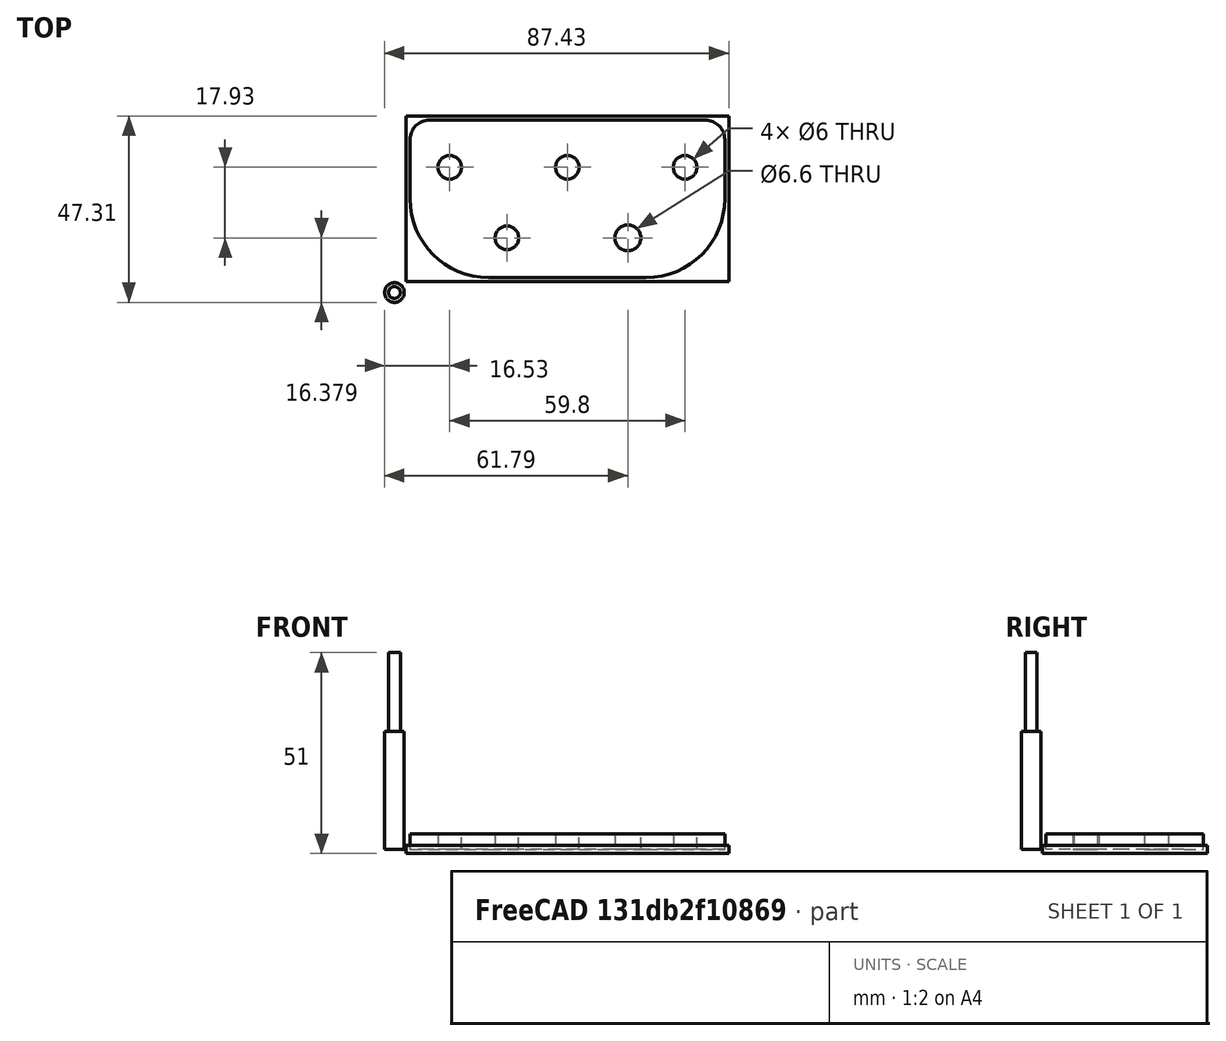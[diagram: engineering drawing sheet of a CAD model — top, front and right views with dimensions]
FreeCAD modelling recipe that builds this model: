
FCSTD DOCUMENT  (FreeCAD 1.0R39319 (Git))
Label: HousingAtari_MINI_BUTTONS_RETROFIT
License: All rights reserved
LicenseURL: https://en.wikipedia.org/wiki/All_rights_reserved
objects: App::DocumentObjectGroup×3, Path::FeaturePython×3, Sketcher::SketchObject×2, Part::FeaturePython×2, PartDesign::Pad×1, PartDesign::Body×1, App::FeaturePython×1, Part::Part2DObjectPython×1, Mesh::FeaturePython×1
note: 11 computed .brp shape members not serialized (recipe doc carries the construction recipe); baked Part::Feature solids carry a one-line shape summary decoded from their .brp

FEATURE [Sketcher::SketchObject] Sketch  label="A3"
  ArcFitTolerance = 0
  FullyConstrained = false
  MakeInternals = false
  MapMode = 5
  sketch-geometry (7):
    g0: LineSegment StartX=0 StartY=420 StartZ=0 EndX=0 EndY=0 EndZ=0
    g1: LineSegment StartX=0 StartY=420 StartZ=0 EndX=148.5 EndY=420 EndZ=0
    g2: LineSegment StartX=148.5 StartY=420 StartZ=0 EndX=148.5 EndY=0 EndZ=0
    g3: LineSegment StartX=148.5 StartY=420 StartZ=0 EndX=297 EndY=420 EndZ=0
    g4: LineSegment StartX=297 StartY=420 StartZ=0 EndX=297 EndY=210 EndZ=0
    g5: LineSegment StartX=297 StartY=210 StartZ=0 EndX=297 EndY=0 EndZ=0
    g6: LineSegment StartX=297 StartY=210 StartZ=0 EndX=0 EndY=210 EndZ=0
  constraints (21):
    c: Vertical(g0)
    c: DistanceY(g0,g0) = 420
    c: Coincident(g1,g0)
    c: Horizontal(g1)
    c: Coincident(g2,g1)
    c: Coincident(g3,g1)
    c: Horizontal(g3)
    c: Equal(g1,g3)
    c: Vertical(g2)
    c: DistanceX(g0,g3) = 297
    c: Coincident(g4,g3)
    c: Vertical(g4)
    c: Coincident(g5,g4)
    c: PointOnObject(g5,g-1)
    c: Vertical(g5)
    c: Equal(g5,g4)
    c: PointOnObject(g0,g-1)
    c: PointOnObject(g0,g-2)
    c: Coincident(g6,g4)
    c: PointOnObject(g6,g0)
    c: Horizontal(g6)
FEATURE [Sketcher::SketchObject] Sketch008  label="PART-mini_switches"
  ArcFitTolerance = 1e-06
  AttachmentSupport = -> [XY_Plane]
  FullyConstrained = false
  MakeInternals = false
  MapMode = 5
  sketch-geometry (24):
    g0: LineSegment StartX=3.9304 StartY=38.8086 StartZ=0 EndX=3.9304 EndY=23.8086 EndZ=0
    g1: LineSegment StartX=23.9304 StartY=3.80861 StartZ=0 EndX=63.9304 EndY=3.80861 EndZ=0
    g2: LineSegment StartX=83.9304 StartY=23.8086 StartZ=0 EndX=83.9304 EndY=38.8086 EndZ=0
    g3: LineSegment StartX=78.9304 StartY=43.8086 StartZ=0 EndX=8.9304 EndY=43.8086 EndZ=0
    g4: ArcOfCircle CenterX=23.9304 CenterY=23.8086 CenterZ=0 NormalX=0 NormalY=0 NormalZ=1 AngleXU=0 Radius=20 StartAngle=3.14159 EndAngle=4.71239
    g5: GeomPoint [constr] X=3.9304 Y=3.80861 Z=0
    g6: ArcOfCircle CenterX=63.9304 CenterY=23.8086 CenterZ=0 NormalX=0 NormalY=0 NormalZ=1 AngleXU=0 Radius=20 StartAngle=4.71239 EndAngle=6.28319
    g7: GeomPoint [constr] X=83.9304 Y=3.80861 Z=0
    g8: ArcOfCircle CenterX=78.9304 CenterY=38.8086 CenterZ=0 NormalX=0 NormalY=0 NormalZ=1 AngleXU=0 Radius=5 StartAngle=4e-16 EndAngle=1.5708
    g9: GeomPoint [constr] X=83.9304 Y=43.8086 Z=0
    g10: ArcOfCircle CenterX=8.9304 CenterY=38.8086 CenterZ=0 NormalX=0 NormalY=0 NormalZ=1 AngleXU=0 Radius=5 StartAngle=1.5708 EndAngle=3.14159
    g11: GeomPoint [constr] X=3.9304 Y=43.8086 Z=0
    g12: LineSegment [constr] StartX=14.0304 StartY=31.8086 StartZ=0 EndX=43.9304 EndY=31.8086 EndZ=0
    g13: LineSegment [constr] StartX=43.9304 StartY=31.8086 StartZ=0 EndX=73.8304 EndY=31.8086 EndZ=0
    g14: LineSegment [constr] StartX=73.8304 StartY=31.8086 StartZ=0 EndX=59.2902 EndY=13.8786 EndZ=0
    g15: LineSegment [constr] StartX=59.2902 StartY=13.8786 StartZ=0 EndX=28.5706 EndY=13.8786 EndZ=0
    g16: LineSegment [constr] StartX=28.5706 StartY=13.8786 StartZ=0 EndX=14.0304 EndY=31.8086 EndZ=0
    g17: Circle CenterX=14.0304 CenterY=31.8086 CenterZ=0 NormalX=0 NormalY=0 NormalZ=1 AngleXU=0 Radius=3
    g18: Circle CenterX=43.9304 CenterY=31.8086 CenterZ=0 NormalX=0 NormalY=0 NormalZ=1 AngleXU=0 Radius=3
    g19: Circle CenterX=73.8304 CenterY=31.8086 CenterZ=0 NormalX=0 NormalY=0 NormalZ=1 AngleXU=0 Radius=3
    g20: Circle CenterX=59.2902 CenterY=13.8786 CenterZ=0 NormalX=0 NormalY=0 NormalZ=1 AngleXU=0 Radius=3.30031
    g21: Circle CenterX=28.5706 CenterY=13.8786 CenterZ=0 NormalX=0 NormalY=0 NormalZ=1 AngleXU=0 Radius=3
    g22: LineSegment [constr] StartX=8.9304 StartY=43.8086 StartZ=0 EndX=43.9304 EndY=31.8086 EndZ=0
    g23: LineSegment [constr] StartX=78.9304 StartY=43.8086 StartZ=0 EndX=43.9304 EndY=31.8086 EndZ=0
  constraints (52):
    c: Vertical(g0)
    c: Vertical(g2)
    c: Horizontal(g1)
    c: Horizontal(g3)
    c: PointOnObject(g5,g0)
    c: PointOnObject(g5,g1)
    c: Tangent(g0,g4) = -1.5708
    c: Tangent(g1,g4) = -1.5708
    c: PointOnObject(g7,g1)
    c: PointOnObject(g7,g2)
    c: Tangent(g1,g6) = -1.5708
    c: Tangent(g2,g6) = -1.5708
    c: Radius(g4) = 20
    c: Equal(g6,g4)
    c: DistanceX(g0,g2) = 80
    c: PointOnObject(g9,g3)
    c: PointOnObject(g9,g2)
    c: Tangent(g3,g8) = -1.5708
    c: Tangent(g2,g8) = -1.5708
    c: PointOnObject(g11,g0)
    c: PointOnObject(g11,g3)
    c: Tangent(g0,g10) = -1.5708
    c: Tangent(g3,g10) = -1.5708
    c: Equal(g10,g8)
    c: Horizontal(g12)
    c: Coincident(g13,g12)
    c: Horizontal(g13)
    c: Coincident(g14,g13)
    c: Coincident(g15,g14)
    c: Horizontal(g15)
    c: Coincident(g16,g15)
    c: Equal(g16,g14)
    c: DistanceY(g1,g3) = 40
    c: Equal(g13,g12)
    c: Coincident(g16,g12)
    c: Coincident(g17,g12)
    c: Coincident(g18,g12)
    c: Coincident(g19,g13)
    c: Coincident(g20,g14)
    c: Coincident(g21,g15)
    c: Equal(g18,g19)
    c: Equal(g19,g21)
    c: Diameter(g17) = 6
    c: Equal(g17,g21)
    c: Coincident(g22,g3)
    c: Coincident(g22,g12)
    c: Coincident(g23,g3)
    c: Coincident(g23,g12)
    c: Equal(g23,g22)
    c: DistanceY(g12,g3) = 12
    c: DistanceY(g14,g13) = 17.93
    c: Radius(g8) = 5
FEATURE [PartDesign::Pad] Pad
  Direction = (0,0,1)
  Length = 4
  Length2 = 10
  Profile = -> Sketch008
  ReferenceAxis = -> Sketch008 [N_Axis]
  Refine = true
  Suppressed = false
  Type = 0
FEATURE [PartDesign::Body] Body
  AllowCompound = false
  Group = -> [Sketch,Pad,Sketch008]
  Origin = -> Origin
  Tip = -> Pad
FEATURE [App::FeaturePython] SetupSheet  # Path/CAM operation (typed FeaturePython)
  ClearanceHeightExpression = OpStockZMax+SetupSheet.ClearanceHeightOffset
  ClearanceHeightOffset = 5
  CoolantMode = 0
  CoolantModes = None | Flood | Mist
  FinalDepthExpression = OpFinalDepth
  HorizRapid = 0
  SafeHeightExpression = OpStockZMax+SetupSheet.SafeHeightOffset
  SafeHeightOffset = 3
  StartDepthExpression = OpStartDepth
  StepDownExpression = OpToolDiameter
  VertRapid = 0
FEATURE [Part::Part2DObjectPython] Clone2D  label="Model-PART-mini_switches"  # Draft 2D object (typed FeaturePython)
  Fuse = false
  Objects = -> [Sketch008]
  PathResource = Model
  Scale = (1,1,1)
FEATURE [App::DocumentObjectGroup] Model
  Group = -> [Clone2D]
FEATURE [Part::FeaturePython] ToolBit  label="Endmill"  # Path/CAM toolbit (typed FeaturePython)
  BitPropertyNames = Chipload | CuttingEdgeHeight | Diameter | Flutes | Length | Material | ShankDiameter | SpindleDirection
  BitShape = <path>
  Chipload = 0
  CuttingEdgeHeight = 30
  Diameter = 5
  Flutes = 0
  Length = 50
  Material = 0
  ShankDiameter = 3
  ShapeName = endmill
  SpindleDirection = 0
FEATURE [Path::FeaturePython] TC__Default_Tool  label="TC: Default Tool"  # Path/CAM operation (typed FeaturePython)
  HorizFeed = 0
  HorizRapid = 0
  SpindleDir = 0
  SpindleSpeed = 0
  Tool = -> ToolBit
  ToolNumber = 1
  VertFeed = 0
  VertRapid = 0
  expr: HorizRapid = SetupSheet.HorizRapid
  expr: VertRapid = SetupSheet.VertRapid
FEATURE [App::DocumentObjectGroup] Tools
  Group = -> [TC__Default_Tool]
FEATURE [Part::FeaturePython] Stock  # WARN: FeaturePython — macro-defined, semantics opaque (R4)
  Base = -> Model
  ExtXneg = 1
  ExtXpos = 1
  ExtYneg = 1
  ExtYpos = 1
  ExtZneg = 1
  ExtZpos = 1
  Placement = pos=(3.9304,3.80861,0) rot=(0,0,1;0rad)
  StockType = FromBase
FEATURE [Path::FeaturePython] Engrave  # Path/CAM operation (typed FeaturePython)
  Active = true
  Base = -> [Clone2D]
  ClearanceHeight = 6
  CoolantMode = 0
  CycleTime = Cycletime Error
  FinalDepth = -5
  OpFinalDepth = -5
  OpStartDepth = 0
  OpStockZMax = 1
  OpStockZMin = -1
  OpToolDiameter = 5
  SafeHeight = 4
  StartDepth = 0
  StartVertex = 0
  StepDown = 5
  ToolController = -> TC__Default_Tool
  expr: ClearanceHeight = OpStockZMax + SetupSheet.ClearanceHeightOffset
  expr: FinalDepth = OpFinalDepth
  expr: SafeHeight = OpStockZMax + SetupSheet.SafeHeightOffset
  expr: StartDepth = OpStartDepth
  expr: StepDown = OpToolDiameter
FEATURE [App::DocumentObjectGroup] Operations
  Group = -> [Engrave]
FEATURE [Path::FeaturePython] Job  # Path/CAM operation (typed FeaturePython)
  CycleTime = 00:00:00
  Fixtures = G54
  GeometryTolerance = 0.01
  JobType = 0
  Model = -> Model
  Operations = -> Operations
  OrderOutputBy = 0
  PostProcessor = 1
  SetupSheet = -> SetupSheet
  SplitOutput = false
  Stock = -> Stock
  Tools = -> Tools
FEATURE [Mesh::FeaturePython] CutMaterial  # WARN: FeaturePython — macro-defined, semantics opaque (R4)
note: 1 file-system path scrubbed to <path> (originals preserved in the JSON sidecar)
